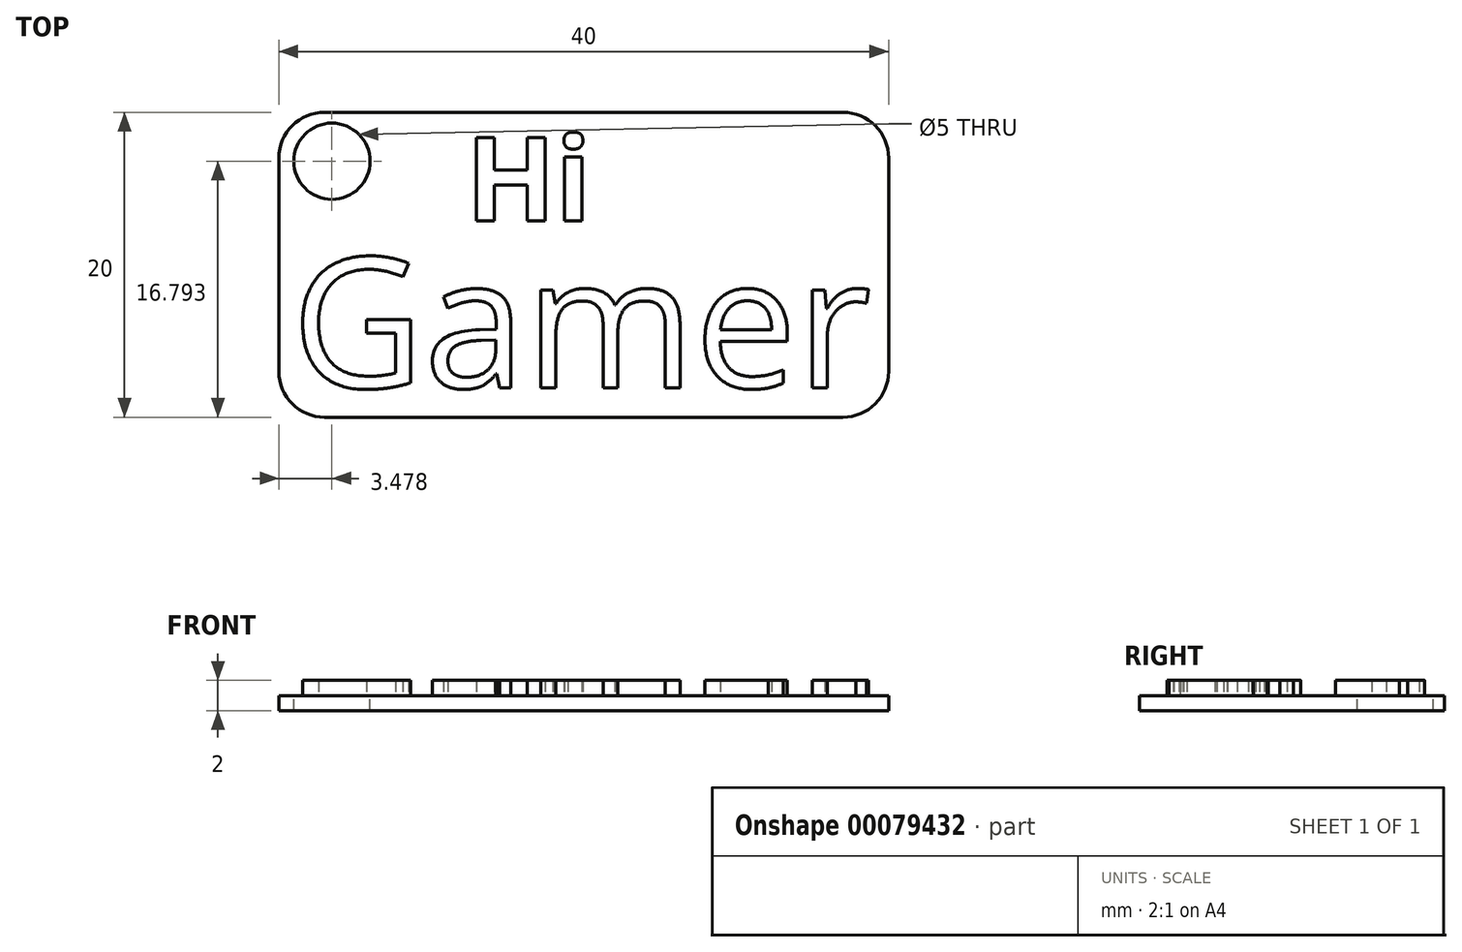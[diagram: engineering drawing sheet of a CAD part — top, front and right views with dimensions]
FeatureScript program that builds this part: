
annotation { "Feature Type Name" : "Feature", "Feature Type Description" : "" }
export const myFeature = defineFeature(function(context is Context, id is Id, definition is map)
    precondition{}
    {
        {
            var Q0;
            Q0=qCreatedBy(makeId("Top.planeOp"),FACE);
            var sketch = newSketch(context, id + "F0", { "sketchPlane" : qUnion([Q0])});
            skLineSegment(sketch, "E0.bottom", {"start": v(-20, -10) * mm, "end": v(20, -10) * mm});
            skLineSegment(sketch, "E0.top", {"start": v(-20, 10) * mm, "end": v(20, 10) * mm});
            skLineSegment(sketch, "E0.left", {"start": v(-20, -10) * mm, "end": v(-20, 10) * mm});
            skLineSegment(sketch, "E0.right", {"start": v(20, -10) * mm, "end": v(20, 10) * mm});
            skPoint(sketch, "E0.middle", {"position": v(0, 0) * mm});
            skSolve(sketch);
        }
        {
            var Q0;
            Q0=makeQuery(id+"F0.imprint","IMPRINT",FACE,{"disambiguationData":[TD([[makeQuery(id+"F0.imprint","IMPRINT",EDGE,{"derivedFrom":sQuery(id+"F0.wireOp",EDGE,"E0.bottom")}),1.0]])]});
            extrude(context, id + "F1", {"entities" : qUnion([Q0]), "depth" : 1 * mm});
        }
        {
            var Q0;
            Q0=makeQuery(id+"F1.opExtrude","SWEPT_EDGE",EDGE,{"disambiguationData":[OSD([sQuery(id+"F0.wireOp",EDGE,"E0.top"),sQuery(id+"F0.wireOp",EDGE,"E0.left")])]});
            var Q1;
            Q1=makeQuery(id+"F1.opExtrude","SWEPT_EDGE",EDGE,{"disambiguationData":[OSD([sQuery(id+"F0.wireOp",EDGE,"E0.bottom"),sQuery(id+"F0.wireOp",EDGE,"E0.left")])]});
            var Q2;
            Q2=makeQuery(id+"F1.opExtrude","SWEPT_EDGE",EDGE,{"disambiguationData":[OSD([sQuery(id+"F0.wireOp",EDGE,"E0.bottom"),sQuery(id+"F0.wireOp",EDGE,"E0.right")])]});
            var Q3;
            Q3=makeQuery(id+"F1.opExtrude","SWEPT_EDGE",EDGE,{"disambiguationData":[OSD([sQuery(id+"F0.wireOp",EDGE,"E0.top"),sQuery(id+"F0.wireOp",EDGE,"E0.right")])]});
            fillet(context, id + "F2", {"entities" : qUnion([Q0, Q1, Q2, Q3]), "radius" : 3 * mm, "tangentPropagation" : true, "allowEdgeOverflow" : false});
        }
        {
            var Q0;
            Q0=makeQuery(id+"F1.opExtrude","CAP_FACE",FACE,{"disambiguationData":[OSD([sQuery(id+"F0.wireOp",EDGE,"E0.bottom"),sQuery(id+"F0.wireOp",EDGE,"E0.top"),sQuery(id+"F0.wireOp",EDGE,"E0.left"),sQuery(id+"F0.wireOp",EDGE,"E0.right")])],"isStart":false});
            var sketch = newSketch(context, id + "F3", { "sketchPlane" : qUnion([Q0])});
            skText(sketch, "E1", { "text": "Gamer", "fontName": "OpenSans-Regular.ttf"});
            const initialGuessF3  = {"E1": [-0.01917, -0.00806, 1, 0, 0.0086]};
            skSetInitialGuess(sketch, initialGuessF3);
            skSolve(sketch);
        }
        {
            var Q0;
            Q0 = qSketchRegion(id + "F3", true);
            extrude(context, id + "F4", {"entities" : qUnion([Q0]), "operationType" : NewBodyOperationType.ADD, "depth" : 1 * mm});
        }
        {
            var Q0;
            {var subQ0=sQuery(id+"F0.wireOp",EDGE,"E0.left");var subQ1=sQuery(id+"F0.wireOp",EDGE,"E0.bottom");var subQ2=sQuery(id+"F0.wireOp",EDGE,"E0.right");var subQ3=sQuery(id+"F0.wireOp",EDGE,"E0.top");Q0=makeQuery(id+"F4.boolean.opBoolean","SPLIT",FACE,{"disambiguationData":[TD([makeQuery(id+"F1.opExtrude","SWEPT_FACE",FACE,{"disambiguationData":[OSD([subQ1])]})])],"derivedFrom":makeQuery(id+"F1.opExtrude","CAP_FACE",FACE,{"disambiguationData":[OSD([subQ1,subQ3,subQ0,subQ2])],"isStart":false})});}
            var sketch = newSketch(context, id + "F5", { "sketchPlane" : qUnion([Q0])});
            skPoint(sketch, "E2", {"position": v(-16.52, 6.8) * mm});
            skSolve(sketch);
        }
        {
            var Q0;
            Q0=sQuery(id+"F5.wireOp",VERTEX,"E2");
            var Q1;
            Q1=makeQuery(id+"F1.opExtrude","SWEPT_BODY",BODY,{"disambiguationData":[OSD([sQuery(id+"F0.wireOp",EDGE,"E0.bottom"),sQuery(id+"F0.wireOp",EDGE,"E0.top"),sQuery(id+"F0.wireOp",EDGE,"E0.left"),sQuery(id+"F0.wireOp",EDGE,"E0.right")])]});
            hole(context, id + "F6", {"style" : HoleStyle.SIMPLE, "endStyle" : HoleEndStyle.BLIND, "holeDiameter" : 5 * mm, "holeDepth" : 50 * mm, "locations" : qUnion([Q0]), "scope" : qUnion([Q1])});
        }
        {
            var Q0;
            {var subQ0=sQuery(id+"F0.wireOp",EDGE,"E0.left");var subQ1=sQuery(id+"F0.wireOp",EDGE,"E0.bottom");var subQ2=sQuery(id+"F0.wireOp",EDGE,"E0.right");var subQ3=sQuery(id+"F0.wireOp",EDGE,"E0.top");Q0=makeQuery(id+"F4.boolean.opBoolean","SPLIT",FACE,{"disambiguationData":[TD([makeQuery(id+"F1.opExtrude","SWEPT_FACE",FACE,{"disambiguationData":[OSD([subQ1])]})])],"derivedFrom":makeQuery(id+"F1.opExtrude","CAP_FACE",FACE,{"disambiguationData":[OSD([subQ1,subQ3,subQ0,subQ2])],"isStart":false})});}
            var sketch = newSketch(context, id + "F7", { "sketchPlane" : qUnion([Q0])});
            skText(sketch, "E3", { "text": "Hi", "fontName": "OpenSans-Bold.ttf"});
            const initialGuessF7  = {"E3": [-0.00773, 0.00287, 1, 0, 0.00553]};
            skSetInitialGuess(sketch, initialGuessF7);
            skSolve(sketch);
        }
        {
            var Q0;
            Q0 = qSketchRegion(id + "F7", true);
            extrude(context, id + "F8", {"entities" : qUnion([Q0]), "operationType" : NewBodyOperationType.ADD, "depth" : 1 * mm});
        }
    });
